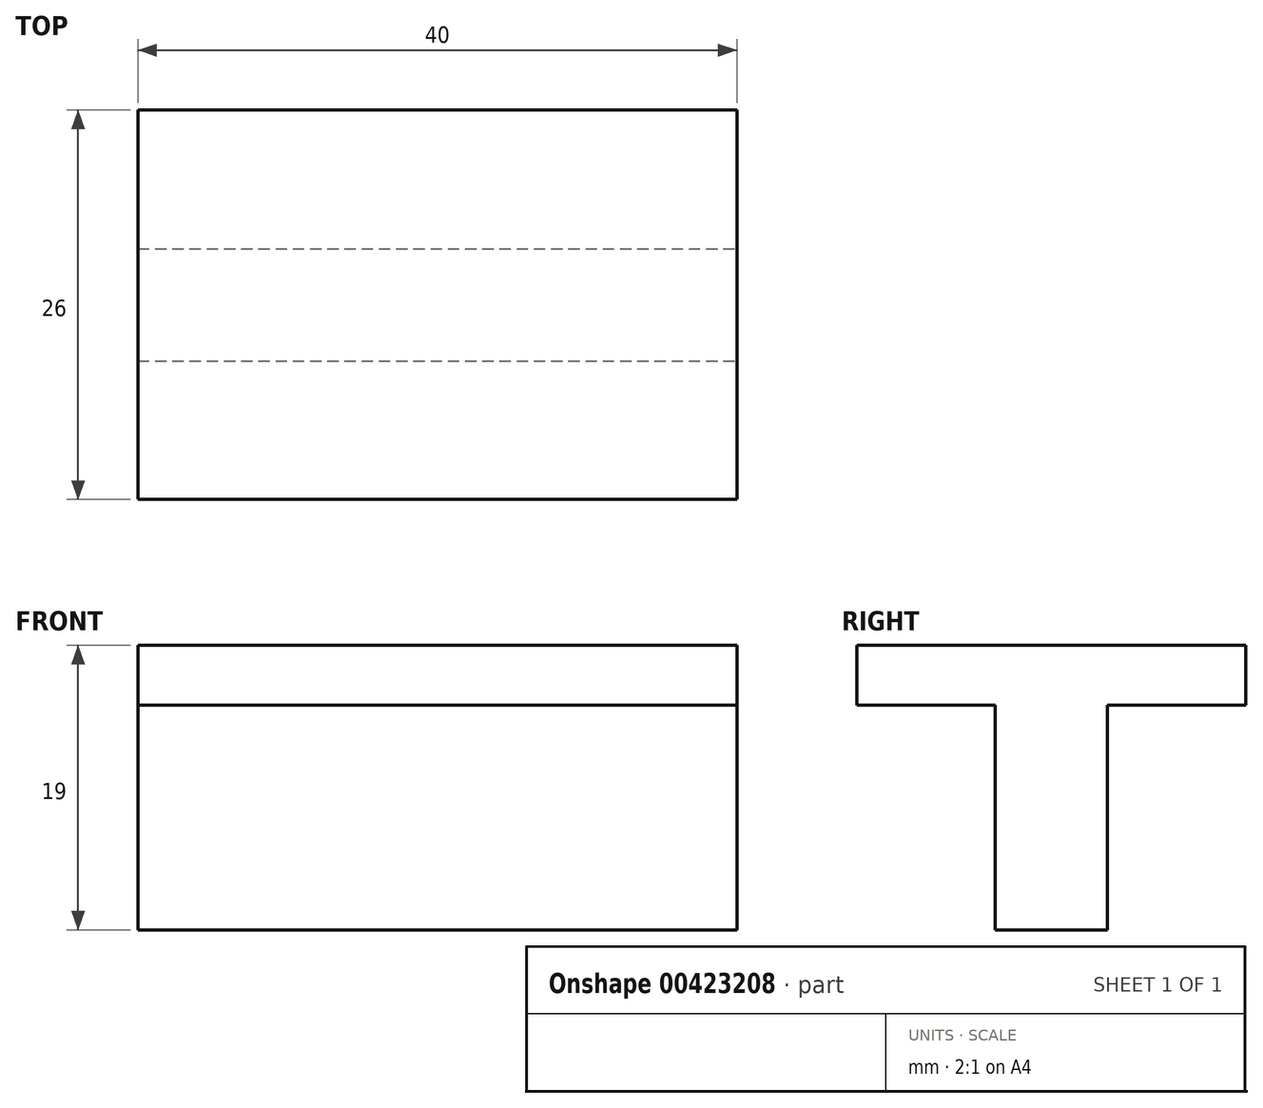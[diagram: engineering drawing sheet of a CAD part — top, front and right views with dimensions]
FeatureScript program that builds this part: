
annotation { "Feature Type Name" : "Feature", "Feature Type Description" : "" }
export const myFeature = defineFeature(function(context is Context, id is Id, definition is map)
    precondition{}
    {
        {
            var Q0;
            Q0=qCreatedBy(makeId("Top.planeOp"),FACE);
            var sketch = newSketch(context, id + "F0", { "sketchPlane" : qUnion([Q0])});
            skLineSegment(sketch, "E0.bottom", {"start": v(-20, 3.75) * mm, "end": v(20, 3.75) * mm});
            skLineSegment(sketch, "E0.top", {"start": v(-20, -3.75) * mm, "end": v(20, -3.75) * mm});
            skLineSegment(sketch, "E0.left", {"start": v(-20, 3.75) * mm, "end": v(-20, -3.75) * mm});
            skLineSegment(sketch, "E0.right", {"start": v(20, 3.75) * mm, "end": v(20, -3.75) * mm});
            skPoint(sketch, "E0.middle", {"position": v(0, 0) * mm});
            skSolve(sketch);
        }
        {
            var Q0;
            Q0=makeQuery(id+"F0.imprint","IMPRINT",FACE,{"disambiguationData":[TD([[makeQuery(id+"F0.imprint","IMPRINT",EDGE,{"derivedFrom":sQuery(id+"F0.wireOp",EDGE,"E0.bottom")}),-1.0]])]});
            extrude(context, id + "F1", {"entities" : qUnion([Q0]), "depth" : 15 * mm, "offsetDistance" : 25 * mm});
        }
        {
            var Q0;
            Q0=makeQuery(id+"F1.opExtrude","CAP_FACE",FACE,{"disambiguationData":[OSD([sQuery(id+"F0.wireOp",EDGE,"E0.bottom"),sQuery(id+"F0.wireOp",EDGE,"E0.top"),sQuery(id+"F0.wireOp",EDGE,"E0.left"),sQuery(id+"F0.wireOp",EDGE,"E0.right")])],"isStart":false});
            var sketch = newSketch(context, id + "F2", { "sketchPlane" : qUnion([Q0])});
            skLineSegment(sketch, "E1.bottom", {"start": v(-20, 13) * mm, "end": v(20, 13) * mm});
            skLineSegment(sketch, "E1.top", {"start": v(-20, -13) * mm, "end": v(20, -13) * mm});
            skLineSegment(sketch, "E1.left", {"start": v(-20, 13) * mm, "end": v(-20, -13) * mm});
            skLineSegment(sketch, "E1.right", {"start": v(20, 13) * mm, "end": v(20, -13) * mm});
            skPoint(sketch, "E1.middle", {"position": v(0, 0) * mm});
            skSolve(sketch);
        }
        {
            var Q0;
            {var subQ0=sQuery(id+"F2.wireOp",EDGE,"E1.bottom");Q0=makeQuery(id+"F2.imprint","IMPRINT",FACE,{"disambiguationData":[TD([[makeQuery(id+"F2.imprint","IMPRINT",EDGE,{"derivedFrom":subQ0}),-1.0]])]});}
            var Q1;
            {var subQ1=makeQuery(id+"F1.opExtrude","CAP_EDGE",EDGE,{"disambiguationData":[OSD([sQuery(id+"F0.wireOp",EDGE,"E0.bottom")])],"isStart":false});Q1=makeQuery(id+"F2.imprint","IMPRINT",FACE,{"disambiguationData":[TD([[makeQuery(id+"F2.imprint","IMPRINT",EDGE,{"derivedFrom":subQ1}),-1.0]])]});}
            var Q2;
            {var subQ0=sQuery(id+"F2.wireOp",EDGE,"E1.top");Q2=makeQuery(id+"F2.imprint","IMPRINT",FACE,{"disambiguationData":[TD([[makeQuery(id+"F2.imprint","IMPRINT",EDGE,{"derivedFrom":subQ0}),1.0]])]});}
            extrude(context, id + "F3", {"entities" : qUnion([Q0, Q1, Q2]), "operationType" : NewBodyOperationType.ADD, "depth" : 4 * mm, "offsetDistance" : 25 * mm});
        }
    });
